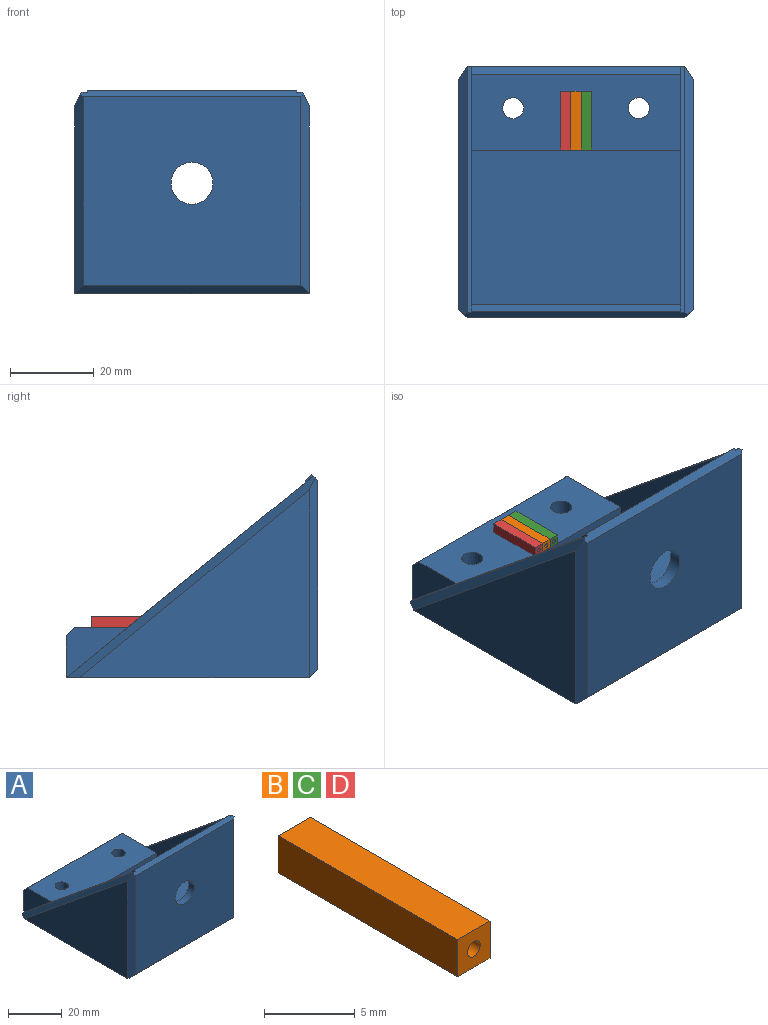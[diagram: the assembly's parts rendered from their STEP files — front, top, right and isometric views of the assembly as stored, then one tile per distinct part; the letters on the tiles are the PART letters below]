
ASSEMBLY  parts=4 mates=3
PART A: 28 faces, bbox 56x60x48.5 mm
  f0: plane 1.95x1.9mm, normal (-1,0,0), area 1mm2, adj f10,f17,f20,f22
  f1: plane 1.95x1.9mm, normal (1,0,0), area 1mm2, adj f10,f14,f20,f22
  f2: plane 58x56mm, normal (0,0,-1), area 3202.4mm2, adj f8,f12,f13,f14,f15,f17,f18,f21
  f3: plane 50x18mm, normal (0,0,1), area 860.7mm2, adj f5,f7,f11,f12,f13,f16,f19,f27
  f4: plane 50x37mm, normal (0,0,1), area 1850mm2, adj f10,f11,f16,f19
  f5: plane 14.69x12mm, normal (-1,0,0), area 86.2mm2, adj f3,f8,f17,f27
  f6: plane 52x45mm, normal (0,-1,0), area 2261.5mm2, adj f9,f22,f24,f25,f26
  f7: plane 14.69x12mm, normal (1,0,0), area 86.2mm2, adj f3,f8,f14,f27
  f8: plane 50x10mm, normal (0,1,0), area 500mm2, adj f2,f5,f7,f27
  f9: cylinder r=5mm len=10mm, axis (0,-1,0), area 94.2mm2, adj f6,f10
  f10: plane 50x38mm, normal (0,1,0), area 1821.5mm2, adj f0,f1,f4,f9,f16,f19,f20
  f11: plane 50x3mm, normal (0,-1,0), area 150mm2, adj f3,f4,f16,f19
  f12: cylinder r=2.5mm len=12mm, axis (0,0,1), area 188.5mm2, adj f2,f3
  f13: cylinder r=2.5mm len=12mm, axis (0,0,1), area 188.5mm2, adj f2,f3
  f14: plane 58.9x48.1mm, normal (0,0.63,0.77), area 76mm2, adj f1,f2,f7,f16,f22,f23
  f15: plane 54.84x44.78mm, normal (1,0,0), area 1227.9mm2, adj f2,f23,f25
  f16: plane 42.31x37.55mm, normal (-1,0,0), area 841.8mm2, adj f3,f4,f10,f11,f14
  f17: plane 58.9x48.1mm, normal (0,0.63,0.77), area 76mm2, adj f0,f2,f5,f19,f21,f22
  f18: plane 54.84x44.78mm, normal (-1,0,0), area 1227.9mm2, adj f2,f21,f24
  f19: plane 42.31x37.55mm, normal (1,0,0), area 841.8mm2, adj f3,f4,f10,f11,f17
  f20: plane 50x1.5mm, normal (0,0.71,0.71), area 106.1mm2, adj f0,f1,f10,f22
  f21: plane 59.36x48.1mm, normal (-0.71,0.45,0.55), area 209mm2, adj f2,f17,f18,f22,f24
  f22: plane 53.29x1.5mm, normal (0,-0.71,0.71), area 110.2mm2, adj f0,f1,f6,f14,f17,f20,f21,f23
  f23: plane 59.36x48.1mm, normal (0.71,0.45,0.55), area 209mm2, adj f2,f14,f15,f22,f25
  f24: plane 47.64x2mm, normal (-0.71,-0.71,0), area 128.9mm2, adj f6,f18,f21,f22,f26
  f25: plane 47.64x2mm, normal (0.71,-0.71,0), area 128.9mm2, adj f6,f15,f22,f23,f26
  f26: plane 56x2mm, normal (0,-0.71,-0.71), area 152.7mm2, adj f2,f6,f24,f25
  f27: plane 50x2mm, normal (0,0.71,0.71), area 141.4mm2, adj f3,f5,f7,f8
PART B: 8 faces, bbox 2.5x14x2.5 mm
  f0: plane 14x2.5mm, normal (-1,0,0), area 35mm2, adj f1,f3,f4,f5
  f1: plane 2.5x2.5mm, normal (0,-1,0), area 5.5mm2, adj f0,f2,f4,f5,f6
  f2: plane 14x2.5mm, normal (1,0,0), area 35mm2, adj f1,f3,f4,f5
  f3: plane 2.5x2.5mm, normal (0,1,0), area 6.2mm2, adj f0,f2,f4,f5
  f4: plane 14x2.5mm, normal (0,0,1), area 35mm2, adj f0,f1,f2,f3
  f5: plane 14x2.5mm, normal (0,0,-1), area 35mm2, adj f0,f1,f2,f3
  f6: cylinder r=0.5mm len=6mm, axis (0,-1,0), area 18.8mm2, adj f1,f7
  f7: plane 1x1mm, normal (0,-1,0), area 0.8mm2, adj f6
PART C: same geometry as B
PART D: same geometry as B
PLACE A at identity
PLACE B t=(23.75,40,12)mm
PLACE C t=(26.25,40,12)mm
PLACE D t=(21.25,40,12)mm
MATE fastened C.f5 <-> A.f3  axis (0,0,-1) through (28.75,40,12)mm
MATE fastened D.f4 <-> B.f4  axis (0,0,1) through (23.75,54,14.5)mm
MATE fastened B.f4 <-> C.f4  axis (0,0,1) through (26.25,54,14.5)mm
